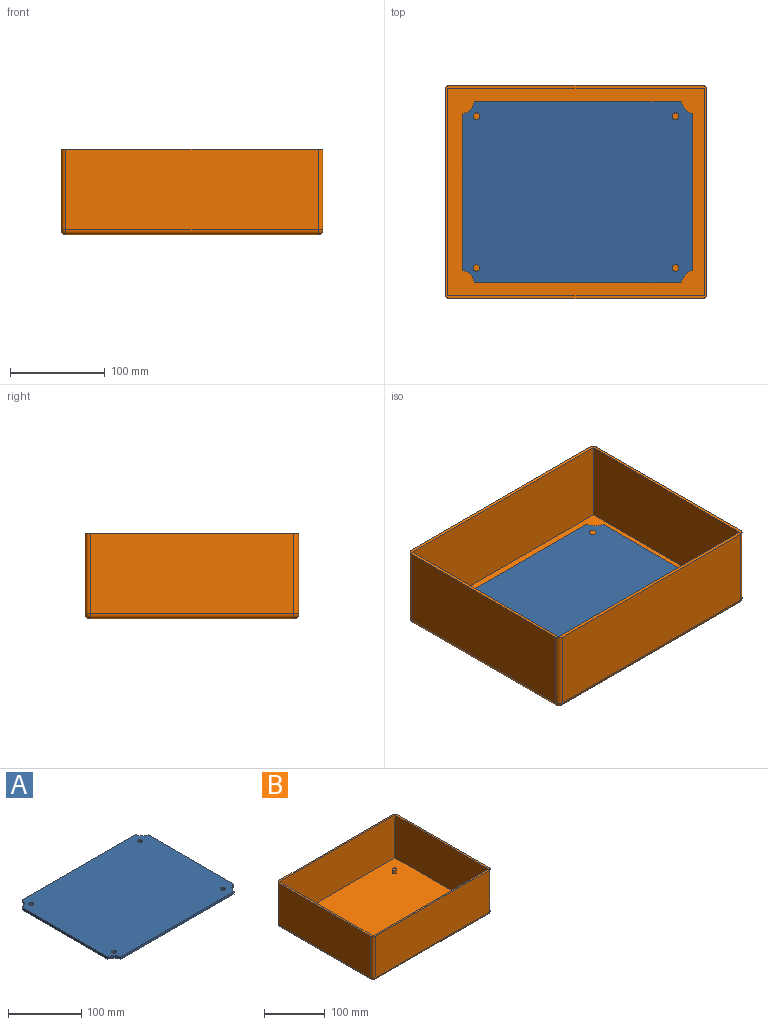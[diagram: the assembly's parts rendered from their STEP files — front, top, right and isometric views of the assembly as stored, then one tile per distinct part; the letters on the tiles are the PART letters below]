
ASSEMBLY  parts=2 mates=1
PART A: 14 faces, bbox 243.1x191x4.1 mm
  f0: cylinder r=16.53mm len=12.95mm, axis (0,0,-1), area 77.2mm2, adj f1,f7,f12,f13
  f1: plane 218.19x4.06mm, normal (0,1,0), area 886.7mm2, adj f0,f2,f12,f13
  f2: cylinder r=14.47mm len=12.95mm, axis (0,0,-1), area 78.8mm2, adj f1,f3,f12,f13
  f3: plane 165.1x4.06mm, normal (-1,0,0), area 671mm2, adj f2,f4,f12,f13
  f4: cylinder r=14.47mm len=12.95mm, axis (0,0,-1), area 78.8mm2, adj f3,f5,f12,f13
  f5: plane 218.19x4.06mm, normal (0,-1,0), area 886.7mm2, adj f4,f6,f12,f13
  f6: cylinder r=16.53mm len=12.95mm, axis (0,0,-1), area 77.2mm2, adj f5,f7,f12,f13
  f7: plane 165.1x4.06mm, normal (1,0,0), area 671mm2, adj f0,f6,f12,f13
  f8: cylinder r=3.51mm len=7.01mm, axis (0,0,-1), area 89.5mm2, adj f12,f13
  f9: cylinder r=3.51mm len=7.01mm, axis (0,0,-1), area 89.5mm2, adj f12,f13
  f10: cylinder r=3.51mm len=7.01mm, axis (0,0,-1), area 89.5mm2, adj f12,f13
  f11: cylinder r=3.51mm len=7.01mm, axis (0,0,-1), area 89.5mm2, adj f12,f13
  f12: plane 243.08x191.01mm, normal (0,0,1), area 45811.7mm2, adj f0,f1,f2,f3,f4,f5,f6,f7
  f13: plane 243.08x191.01mm, normal (0,0,-1), area 45811.7mm2, adj f0,f1,f2,f3,f4,f5,f6,f7
PART B: 31 faces, bbox 276.1x225x89.9 mm
  f0: plane 218.95x86.87mm, normal (-1,0,0), area 19019.6mm2, adj f1,f7,f8,f10
  f1: plane 270x86.87mm, normal (0,1,0), area 23454.5mm2, adj f0,f2,f8,f10
  f2: plane 218.95x86.87mm, normal (1,0,0), area 19019.6mm2, adj f1,f7,f8,f10
  f3: plane 214.88x84.84mm, normal (1,0,0), area 18229.9mm2, adj f8,f24,f28,f30
  f4: plane 265.94x84.84mm, normal (0,1,0), area 22561.1mm2, adj f8,f21,f27,f30
  f5: plane 214.88x84.84mm, normal (-1,0,0), area 18229.9mm2, adj f8,f19,f21,f22
  f6: plane 265.94x84.84mm, normal (0,-1,0), area 22561.1mm2, adj f8,f19,f23,f24
  f7: plane 270x86.87mm, normal (0,-1,0), area 23454.5mm2, adj f0,f2,f8,f10
  f8: plane 276.1x225.04mm, normal (0,0,1), area 2995.6mm2, adj f0,f1,f2,f3,f4,f5,f6,f7
  f9: plane 265.94x214.88mm, normal (0,0,-1), area 57145.8mm2, adj f22,f23,f27,f28
  f10: plane 270x218.95mm, normal (0,0,1), area 58962mm2, adj f0,f1,f2,f7,f12,f14,f16,f18
  f11: plane 7.01x7.01mm, normal (0,0,1), area 38.6mm2, adj f12
  f12: cylinder r=3.51mm len=7.01mm, axis (0,0,-1), area 151mm2, adj f10,f11
  f13: plane 7.01x7.01mm, normal (0,0,1), area 38.6mm2, adj f14
  f14: cylinder r=3.51mm len=7.01mm, axis (0,0,-1), area 151mm2, adj f10,f13
  f15: plane 7.01x7.01mm, normal (0,0,1), area 38.6mm2, adj f16
  f16: cylinder r=3.51mm len=7.01mm, axis (0,0,-1), area 151mm2, adj f10,f15
  f17: plane 7.01x7.01mm, normal (0,0,1), area 38.6mm2, adj f18
  f18: cylinder r=3.51mm len=7.01mm, axis (0,0,-1), area 151mm2, adj f10,f17
  f19: cylinder r=5.08mm len=84.84mm, axis (0,0,1), area 677mm2, adj f5,f6,f8,f20
  f20: sphere r=5.08mm, area 40.5mm2, adj f19,f22,f23
  f21: cylinder r=5.08mm len=84.84mm, axis (0,0,-1), area 677mm2, adj f4,f5,f8,f25
  f22: cylinder r=5.08mm len=214.88mm, axis (0,-1,0), area 1714.7mm2, adj f5,f9,f20,f25
  f23: cylinder r=5.08mm len=265.94mm, axis (1,0,0), area 2122.1mm2, adj f6,f9,f20,f26
  f24: cylinder r=5.08mm len=84.84mm, axis (0,0,-1), area 677mm2, adj f3,f6,f8,f26
  f25: sphere r=5.08mm, area 40.5mm2, adj f21,f22,f27
  f26: sphere r=5.08mm, area 40.5mm2, adj f23,f24,f28
  f27: cylinder r=5.08mm len=265.94mm, axis (-1,0,0), area 2122.1mm2, adj f4,f9,f25,f29
  f28: cylinder r=5.08mm len=214.88mm, axis (0,1,0), area 1714.7mm2, adj f3,f9,f26,f29
  f29: sphere r=5.08mm, area 40.5mm2, adj f27,f28,f30
  f30: cylinder r=5.08mm len=84.84mm, axis (0,0,1), area 677mm2, adj f3,f4,f8,f29
PLACE A t=(-58.4,-84.41,-113.61)mm
PLACE B t=(-60.18,-84.41,-119.45)mm
MATE fastened A.f9 <-> B.f14  axis (0,0,1) through (-165.21,-164.42,-109.54)mm
